# Revit family: H-Line Basin 45cm 1th
name_source: partatom
category: Plumbing Fixtures
units: mm (PartAtom-declared; Revit-internal decimal feet)

## family parameters
Always vertical = Yes
Cut with Voids When Loaded = No
Enable Cutting in Views = No
Host = Wall
Maintain Annotation Orientation = No
OmniClass Number = 23.45.00.00
OmniClass Title = Sanitary, Laundry, and Cleaning Equipment
Part Type = Normal
Room Calculation Point = No
Round Connector Dimension = Use Diameter
Shared = No

## types (2) — shared parameters
Category = Basins – Wall Hung
Ceramic = Ceramic
Colour = White
Fixing Details = Basin Fixing Bolts not supplied, 8mm to 10mm bolts recommended
Manufacturer = Lecico SA
Material = Vitreous China
Silver = Silver
URL = https://www.lecicosa.co.za
zero-valued in all types: Default Elevation

## per-type parameters (varying)
| type | Product code | Technical dimensions | With half pedestal |
| H-Line Basin 45cm 1th | HLIBASWHU1450UE | W451 x H180 x D348mm | No |
| H-Line Basin 45cm 1th - With half pedestal | HLIBASWHU1450UE, MADPEDSEM0000UE | W451 x H470 x D348mm | Yes |

note: column(s) folded — value = type name in every type: Model

## geometry (parser evidence)
native form markers: Sweep x5
no freeform markers — native parametric forms only
